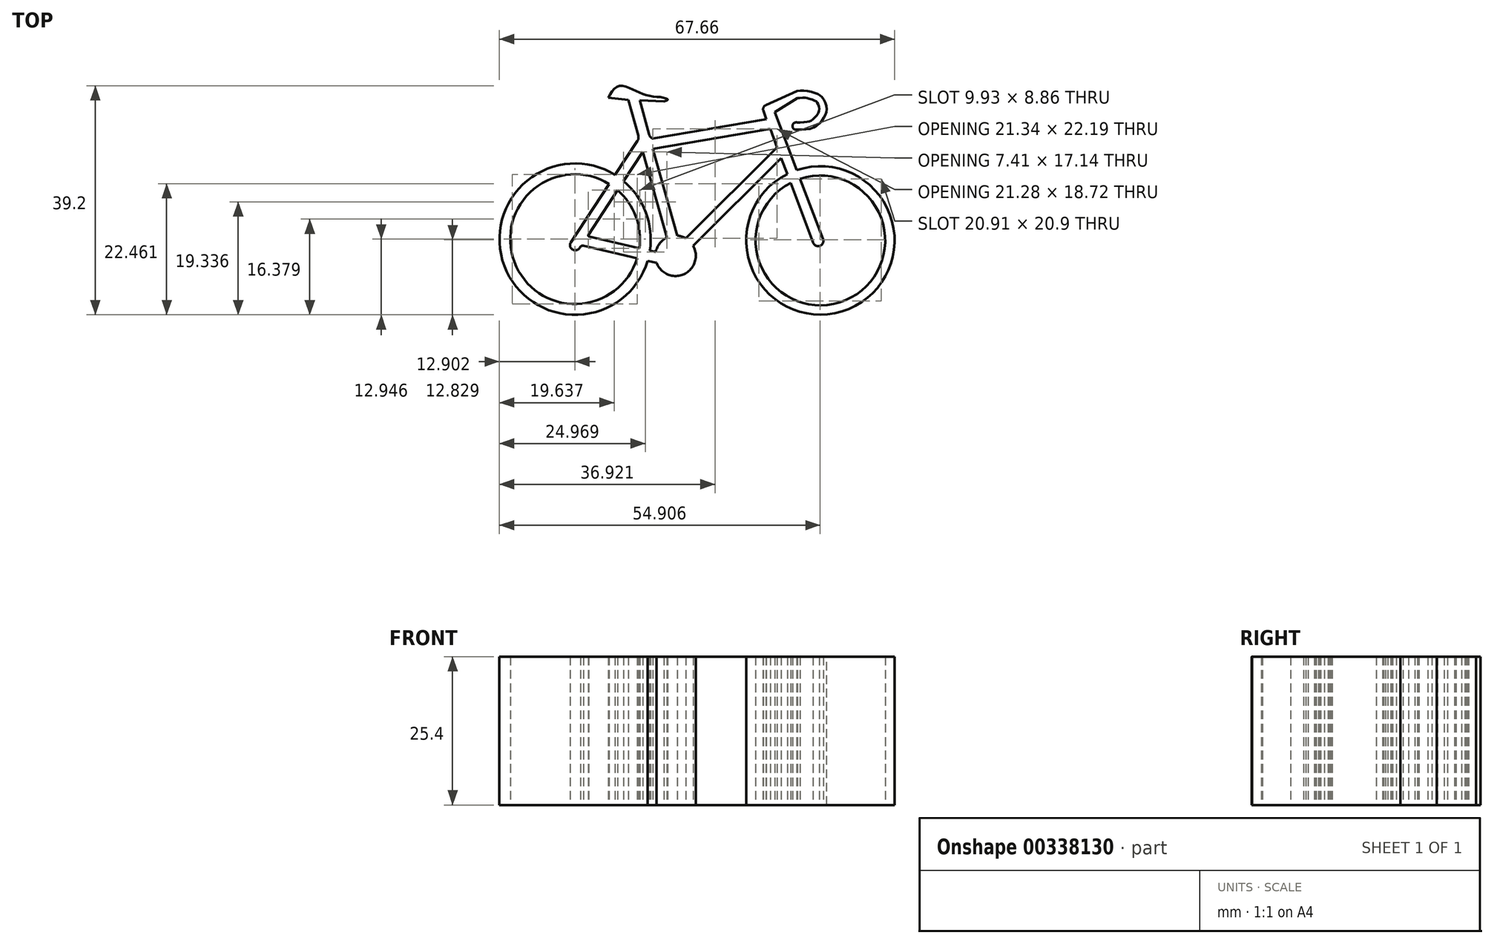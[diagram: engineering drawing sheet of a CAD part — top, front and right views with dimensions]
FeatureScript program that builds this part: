
annotation { "Feature Type Name" : "Feature", "Feature Type Description" : "" }
export const myFeature = defineFeature(function(context is Context, id is Id, definition is map)
    precondition{}
    {
        {
            var Q0;
            Q0=qCreatedBy(makeId("Top.planeOp"),FACE);
            var sketch = newSketch(context, id + "F0", { "sketchPlane" : qUnion([Q0])});
            skLineSegment(sketch, "E0", {"start": v(-87.43, -2.43) * mm, "end": v(-84.4, -2.43) * mm});
            skArc(sketch, "E1", {"start": v(-136.08, -26.87) * mm, "mid": v(-155.06, -42.44) * mm, "end": v(-130.53, -41.55) * mm});
            skLineSegment(sketch, "E2", {"start": v(-132.83, -21.92) * mm, "end": v(-136.08, -26.87) * mm});
            skLineSegment(sketch, "E3.0", {"start": v(-131.34, -22.9) * mm, "end": v(-134.63, -27.92) * mm});
            skArc(sketch, "E4", {"start": v(-143.66, -38.39) * mm, "mid": v(-143.4, -39.62) * mm, "end": v(-142.17, -39.37) * mm});
            skLineSegment(sketch, "E5", {"start": v(-131.34, -22.9) * mm, "end": v(-127.23, -37.57) * mm});
            skLineSegment(sketch, "E6.0", {"start": v(-129.62, -22.43) * mm, "end": v(-125.47, -37.24) * mm});
            skLineSegment(sketch, "E7", {"start": v(-141.23, -39.05) * mm, "end": v(-140.61, -39.2) * mm});
            skLineSegment(sketch, "E8", {"start": v(-140.08, -39.32) * mm, "end": v(-141.53, -38.98) * mm});
            skLineSegment(sketch, "E9", {"start": v(-129.62, -22.43) * mm, "end": v(-109.53, -18.99) * mm});
            skLineSegment(sketch, "E10", {"start": v(-109.53, -18.99) * mm, "end": v(-108.34, -22.15) * mm});
            skLineSegment(sketch, "E11", {"start": v(-109.53, -18.99) * mm, "end": v(-108.8, -20.91) * mm});
            skLineSegment(sketch, "E12", {"start": v(-108.8, -20.91) * mm, "end": v(-109.53, -18.99) * mm});
            skLineSegment(sketch, "E13.0", {"start": v(-108.39, -16.99) * mm, "end": v(-104.97, -26.03) * mm});
            skLineSegment(sketch, "E13.1", {"start": v(-129.65, -20.63) * mm, "end": v(-110.18, -17.3) * mm});
            skArc(sketch, "E14", {"start": v(-128.99, -41.9) * mm, "mid": v(-124.27, -43.84) * mm, "end": v(-122.73, -38.97) * mm});
            skArc(sketch, "E15", {"start": v(-106.6, -26.71) * mm, "mid": v(-96.08, -49.8) * mm, "end": v(-104.97, -26.03) * mm});
            skArc(sketch, "E16", {"start": v(-106.04, -28.22) * mm, "mid": v(-96.65, -48.31) * mm, "end": v(-104.4, -27.53) * mm});
            skArc(sketch, "E17", {"start": v(-137.1, -28.4) * mm, "mid": v(-153.34, -41.75) * mm, "end": v(-132.33, -41.13) * mm});
            skLineSegment(sketch, "E18", {"start": v(-102.97, -36.33) * mm, "end": v(-102.19, -38.4) * mm});
            skLineSegment(sketch, "E19", {"start": v(-101.3, -35.7) * mm, "end": v(-100.5, -37.86) * mm});
            skArc(sketch, "E20", {"start": v(-102.19, -38.4) * mm, "mid": v(-101.05, -39.02) * mm, "end": v(-100.5, -37.86) * mm});
            skArc(sketch, "E21", {"start": v(-141.48, -39) * mm, "mid": v(-141.75, -38.99) * mm, "end": v(-142, -39.1) * mm});
            skArc(sketch, "E22", {"start": v(-140.64, -37.05) * mm, "mid": v(-140.7, -37.22) * mm, "end": v(-140.61, -37.37) * mm});
            skLineSegment(sketch, "E23.trimOffspring", {"start": v(-142, -39.1) * mm, "end": v(-142.17, -39.37) * mm});
            skLineSegment(sketch, "E24.trimOffspring", {"start": v(-129.14, -40.05) * mm, "end": v(-130.14, -39.82) * mm});
            skLineSegment(sketch, "E25.trimOffspring", {"start": v(-128.99, -41.9) * mm, "end": v(-130.53, -41.55) * mm});
            skLineSegment(sketch, "E26.trimOffspring", {"start": v(-123.98, -37.71) * mm, "end": v(-108.34, -22.15) * mm});
            skLineSegment(sketch, "E27.trimOffspring", {"start": v(-122.73, -38.97) * mm, "end": v(-107.65, -23.97) * mm});
            skArc(sketch, "E28.trimOffspring", {"start": v(-131.94, -39.4) * mm, "mid": v(-132.54, -33.96) * mm, "end": v(-135.66, -29.47) * mm});
            skArc(sketch, "E29.trimOffspring", {"start": v(-130.14, -39.82) * mm, "mid": v(-130.82, -33.28) * mm, "end": v(-134.63, -27.92) * mm});
            skLineSegment(sketch, "E30.trimOffspring", {"start": v(-107.65, -23.97) * mm, "end": v(-106.6, -26.71) * mm});
            skLineSegment(sketch, "E31", {"start": v(-119, -35.26) * mm, "end": v(-122.73, -38.97) * mm});
            skLineSegment(sketch, "E32", {"start": v(-132.12, -20.1) * mm, "end": v(-133.27, -15.98) * mm});
            skLineSegment(sketch, "E33", {"start": v(-130.08, -20.72) * mm, "end": v(-130.08, -20.7) * mm});
            skLineSegment(sketch, "E34", {"start": v(-128.87, -20.5) * mm, "end": v(-129.65, -20.63) * mm});
            skArc(sketch, "E35", {"start": v(-132.28, -21.08) * mm, "mid": v(-132.1, -20.6) * mm, "end": v(-132.12, -20.1) * mm});
            skArc(sketch, "E36", {"start": v(-130.33, -19.78) * mm, "mid": v(-130.1, -20.29) * mm, "end": v(-129.65, -20.63) * mm});
            skLineSegment(sketch, "E37.trimOffspring", {"start": v(-130.28, -19.95) * mm, "end": v(-131.34, -15.98) * mm});
            skLineSegment(sketch, "E38", {"start": v(-132.83, -21.92) * mm, "end": v(-132.28, -21.08) * mm});
            skLineSegment(sketch, "E39", {"start": v(-110.18, -17.3) * mm, "end": v(-110.74, -15.81) * mm});
            skLineSegment(sketch, "E40", {"start": v(-110.28, -14.9) * mm, "end": v(-109.43, -14.5) * mm});
            skLineSegment(sketch, "E41", {"start": v(-108.39, -16.99) * mm, "end": v(-108.73, -16.09) * mm});
            skFitSpline(sketch, "E42", {"points": [v(-104.95, -12.47) * mm, v(-103.19, -12.47) * mm, v(-101.42, -13.02) * mm, v(-100.58, -13.63) * mm, v(-99.93, -15.07) * mm, v(-100.02, -16.42) * mm, v(-100.81, -17.72) * mm, v(-102.35, -18.84) * mm, v(-104.95, -19.12) * mm], "startDerivative": vector(13.5, 1.1) * mm, "endDerivative": vector(-17.85, -0.07) * mm});
            skFitSpline(sketch, "E43.0", {"points": [v(-104.85, -13.7) * mm, v(-104.71, -13.7) * mm, v(-104.44, -13.67) * mm, v(-104.07, -13.65) * mm, v(-103.79, -13.66) * mm, v(-103.57, -13.67) * mm, v(-103.4, -13.69) * mm, v(-103.25, -13.72) * mm, v(-103.01, -13.77) * mm, v(-102.7, -13.85) * mm, v(-102.35, -13.98) * mm, v(-102.08, -14.1) * mm, v(-101.89, -14.18) * mm, v(-101.74, -14.25) * mm, v(-101.64, -14.31) * mm, v(-101.6, -14.35) * mm, v(-101.55, -14.41) * mm, v(-101.5, -14.48) * mm, v(-101.43, -14.58) * mm, v(-101.35, -14.74) * mm, v(-101.25, -14.97) * mm, v(-101.16, -15.24) * mm, v(-101.12, -15.46) * mm, v(-101.12, -15.65) * mm, v(-101.14, -15.83) * mm, v(-101.2, -16.02) * mm, v(-101.32, -16.31) * mm, v(-101.5, -16.6) * mm, v(-101.7, -16.84) * mm, v(-101.85, -17.01) * mm, v(-102.04, -17.2) * mm, v(-102.27, -17.4) * mm, v(-102.48, -17.53) * mm, v(-102.65, -17.62) * mm, v(-102.77, -17.67) * mm, v(-102.91, -17.72) * mm, v(-103.13, -17.77) * mm, v(-103.45, -17.82) * mm, v(-104.06, -17.87) * mm, v(-104.59, -17.87) * mm, v(-104.96, -17.87) * mm]});
            skArc(sketch, "E44", {"start": v(-104.96, -17.87) * mm, "mid": v(-105.72, -18.5) * mm, "end": v(-104.95, -19.12) * mm});
            skLineSegment(sketch, "E45", {"start": v(-108.73, -16.09) * mm, "end": v(-104.85, -13.7) * mm});
            skLineSegment(sketch, "E46.trimOffspring", {"start": v(-106.53, -13.18) * mm, "end": v(-104.95, -12.47) * mm});
            skArc(sketch, "E47", {"start": v(-110.28, -14.9) * mm, "mid": v(-110.67, -15.28) * mm, "end": v(-110.74, -15.81) * mm});
            skLineSegment(sketch, "E48", {"start": v(-132.12, -20.1) * mm, "end": v(-133.82, -14) * mm});
            skLineSegment(sketch, "E49", {"start": v(-130.28, -19.95) * mm, "end": v(-131.84, -14.06) * mm});
            skLineSegment(sketch, "E50", {"start": v(-131.84, -14.06) * mm, "end": v(-127.75, -14.3) * mm});
            skLineSegment(sketch, "E51", {"start": v(-137.28, -13.64) * mm, "end": v(-133.82, -14) * mm});
            skLineSegment(sketch, "E52", {"start": v(-109.43, -14.5) * mm, "end": v(-106.53, -13.18) * mm});
            skLineSegment(sketch, "E53.trimOffspring", {"start": v(-135.66, -29.47) * mm, "end": v(-140.67, -37.08) * mm});
            skLineSegment(sketch, "E54.trimOffspring", {"start": v(-137.1, -28.4) * mm, "end": v(-143.66, -38.39) * mm});
            skLineSegment(sketch, "E55.trimOffspring", {"start": v(-131.94, -39.4) * mm, "end": v(-140.61, -37.37) * mm});
            skLineSegment(sketch, "E56.trimOffspring", {"start": v(-132.33, -41.13) * mm, "end": v(-141.23, -39.05) * mm});
            skLineSegment(sketch, "E57.trimOffspring", {"start": v(-106.04, -28.22) * mm, "end": v(-102.46, -37.67) * mm});
            skLineSegment(sketch, "E58.trimOffspring", {"start": v(-104.4, -27.53) * mm, "end": v(-100.8, -37.04) * mm});
            skArc(sketch, "E59.trimOffspring", {"start": v(-127.23, -37.57) * mm, "mid": v(-128.48, -38.58) * mm, "end": v(-129.14, -40.05) * mm});
            skArc(sketch, "E60.trimOffspring", {"start": v(-123.98, -37.71) * mm, "mid": v(-124.7, -37.4) * mm, "end": v(-125.47, -37.24) * mm});
            skLineSegment(sketch, "E61", {"start": v(-133.82, -14) * mm, "end": v(-131.84, -14.06) * mm});
            skFitSpline(sketch, "E62", {"points": [v(-127.75, -14.3) * mm, v(-127.07, -14) * mm, v(-127.75, -13.64) * mm, v(-130.37, -13.29) * mm, v(-133.13, -12.19) * mm, v(-135.61, -11.7) * mm, v(-137.28, -13.64) * mm], "startDerivative": vector(9.57, 2.57) * mm, "endDerivative": vector(-7.45, -13.22) * mm});
            skLineSegment(sketch, "E63", {"start": v(-134.63, -27.92) * mm, "end": v(-131.34, -22.9) * mm});
            skArc(sketch, "E64", {"start": v(-130.14, -39.82) * mm, "mid": v(-130.81, -33.27) * mm, "end": v(-134.63, -27.92) * mm});
            skArc(sketch, "E65", {"start": v(-127.23, -37.57) * mm, "mid": v(-128.46, -38.6) * mm, "end": v(-129.14, -40.05) * mm});
            skLineSegment(sketch, "E66", {"start": v(-130.14, -39.82) * mm, "end": v(-129.14, -40.05) * mm});
            skSolve(sketch);
        }
        {
            var Q0;
            Q0 = qSketchRegion(id + "F0", true);
            extrude(context, id + "F1", {"entities" : qUnion([Q0]), "depth" : 25.4 * mm});
        }
    });
